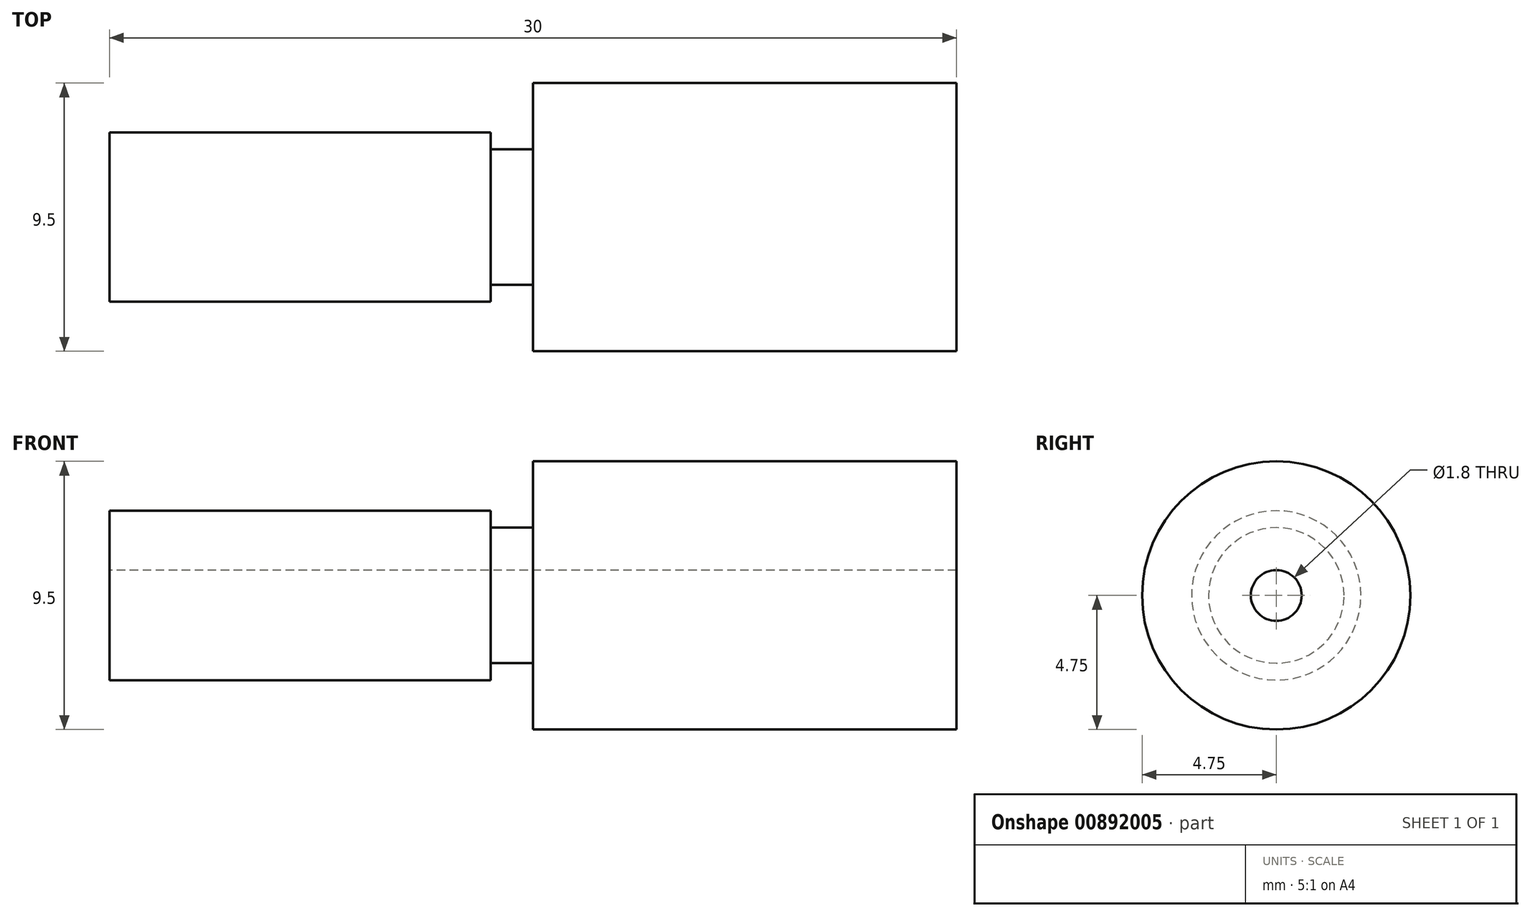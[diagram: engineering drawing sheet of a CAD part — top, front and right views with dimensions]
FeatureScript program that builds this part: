
annotation { "Feature Type Name" : "Feature", "Feature Type Description" : "" }
export const myFeature = defineFeature(function(context is Context, id is Id, definition is map)
    precondition{}
    {
        {
            var Q0;
            Q0=qCreatedBy(makeId("Front.planeOp"),FACE);
            var sketch = newSketch(context, id + "F0", { "sketchPlane" : qUnion([Q0])});
            skLineSegment(sketch, "E0", {"start": v(-1.97, 0) * mm, "end": v(32.41, 0) * mm, "construction": true});
            skLineSegment(sketch, "E1", {"start": v(0, 3) * mm, "end": v(0, 0.9) * mm});
            skLineSegment(sketch, "E2", {"start": v(0, 0.9) * mm, "end": v(30, 0.9) * mm});
            skLineSegment(sketch, "E3", {"start": v(13.5, 2.4) * mm, "end": v(13.5, 3) * mm});
            skLineSegment(sketch, "E4", {"start": v(13.5, 2.4) * mm, "end": v(15, 2.4) * mm});
            skLineSegment(sketch, "E5", {"start": v(15, 2.4) * mm, "end": v(15, 4.75) * mm});
            skLineSegment(sketch, "E6", {"start": v(15, 4.75) * mm, "end": v(30, 4.75) * mm});
            skLineSegment(sketch, "E7.trimOffspring", {"start": v(13.5, 3) * mm, "end": v(0, 3) * mm});
            skLineSegment(sketch, "E8", {"start": v(30, 0.9) * mm, "end": v(30, 4.75) * mm});
            skSolve(sketch);
        }
        {
            var Q0;
            Q0 = qSketchRegion(id + "F0", true);
            var Q1;
            Q1=sQuery(id+"F0.wireOp",EDGE,"E0");
            revolve(context, id + "F1", {"surfaceOperationType" : NewSurfaceOperationType.NEW, "entities" : qUnion([Q0]), "axis" : qUnion([Q1]), "revolveType" : RevolveType.FULL});
        }
    });
